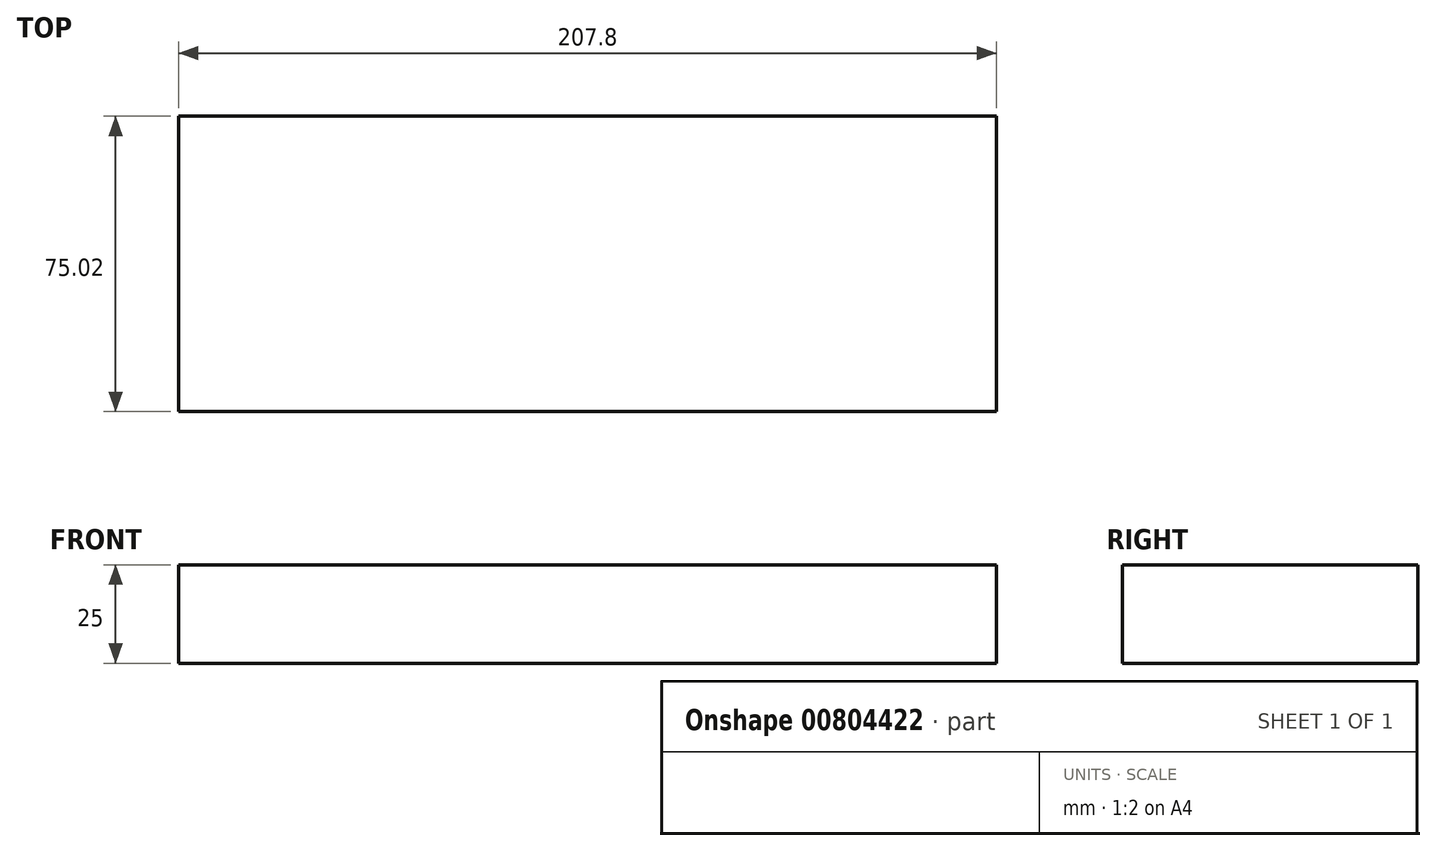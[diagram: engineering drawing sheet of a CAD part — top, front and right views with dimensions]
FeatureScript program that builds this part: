
annotation { "Feature Type Name" : "Feature", "Feature Type Description" : "" }
export const myFeature = defineFeature(function(context is Context, id is Id, definition is map)
    precondition{}
    {
        {
            var Q0;
            Q0=qCreatedBy(makeId("Top.planeOp"),FACE);
            var sketch = newSketch(context, id + "F0", { "sketchPlane" : qUnion([Q0])});
            skLineSegment(sketch, "E0.bottom", {"start": v(-103.9, 37.5) * mm, "end": v(103.9, 37.5) * mm});
            skLineSegment(sketch, "E0.top", {"start": v(-103.9, -37.5) * mm, "end": v(103.9, -37.5) * mm});
            skLineSegment(sketch, "E0.left", {"start": v(-103.9, 37.5) * mm, "end": v(-103.9, -37.5) * mm});
            skLineSegment(sketch, "E0.right", {"start": v(103.9, 37.5) * mm, "end": v(103.9, -37.5) * mm});
            skPoint(sketch, "E0.middle", {"position": v(0, 0) * mm});
            skSolve(sketch);
        }
        {
            var Q0;
            Q0 = qSketchRegion(id + "F0", true);
            extrude(context, id + "F1", {"entities" : qUnion([Q0]), "depth" : 25 * mm, "offsetDistance" : 25 * mm});
        }
    });
